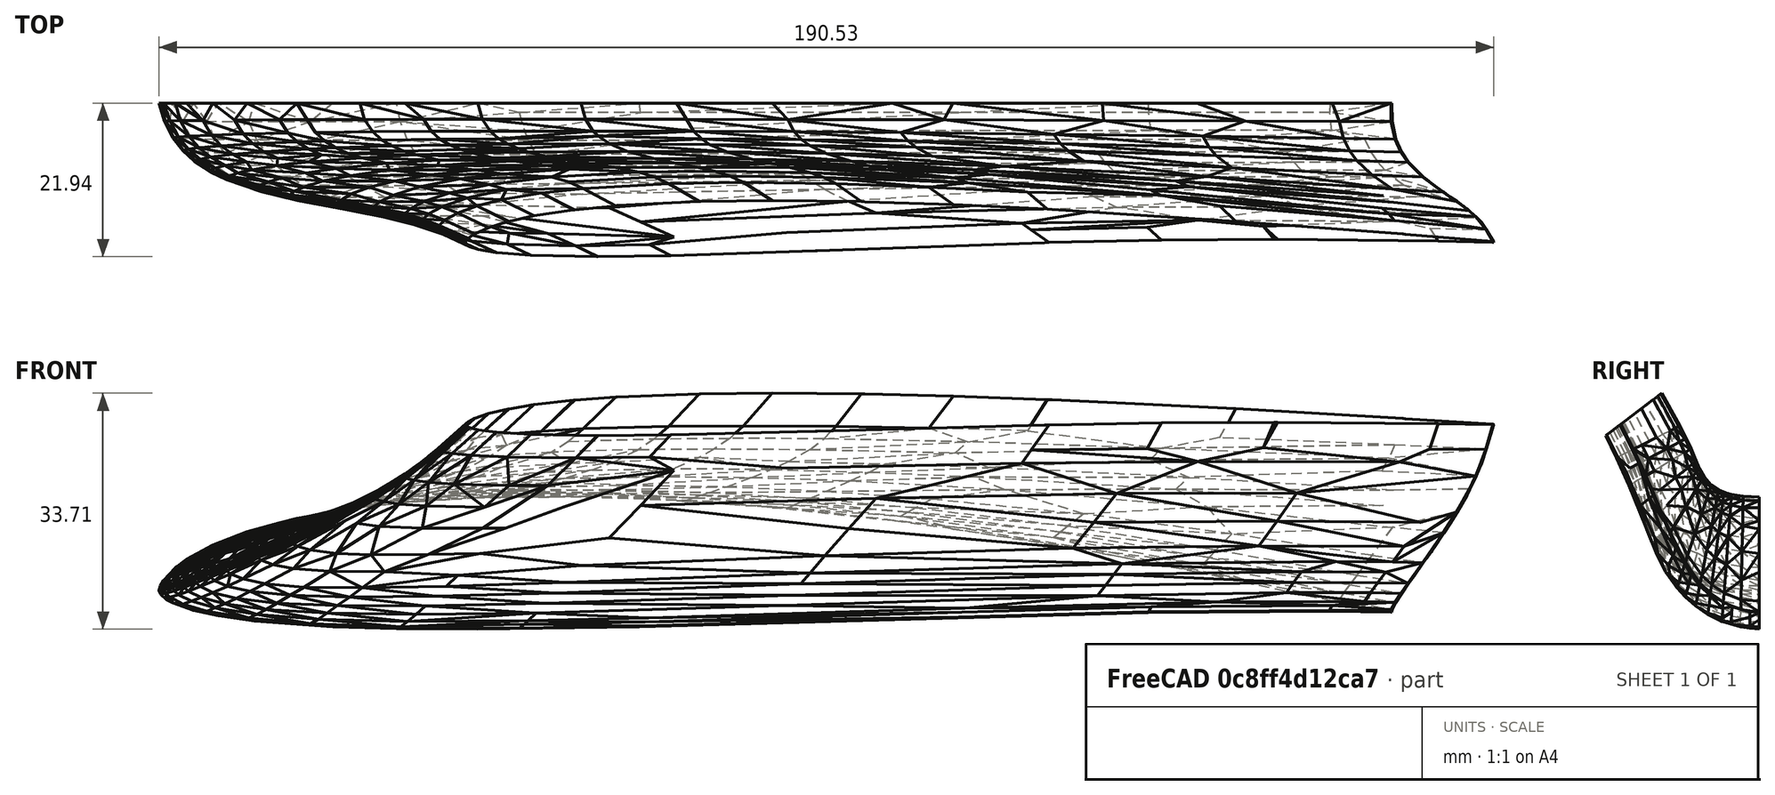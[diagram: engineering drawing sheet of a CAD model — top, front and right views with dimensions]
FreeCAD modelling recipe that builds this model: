
FCSTD DOCUMENT  (FreeCAD 0.19R24276 (Git))
Label: Con_left_winglet_alternative
License: All rights reserved
LicenseURL: http://en.wikipedia.org/wiki/All_rights_reserved
objects: Mesh::Feature×1, Sketcher::SketchObject×1, PartDesign::Body×1, Part::Extrusion×1, Part::Feature×1, Part::MultiCommon×1
note: 5 computed .brp shape members not serialized (recipe doc carries the construction recipe); baked Part::Feature solids carry a one-line shape summary decoded from their .brp

FEATURE [Mesh::Feature] Con_left_winglet_alternative
FEATURE [Sketcher::SketchObject] Sketch
  FullyConstrained = true
  MapMode = 5
  Placement = pos=(0,0,0) rot=(0.57735,0.57735,0.57735;2.0944rad)
  Support = -> [YZ_Plane]
  sketch-geometry (5):
    g0: LineSegment StartX=-958.452 StartY=44.13 StartZ=0 EndX=-927.93 EndY=67.13 EndZ=0
    g1: LineSegment StartX=-927.93 StartY=67.13 StartZ=0 EndX=-887.15 EndY=67.13 EndZ=0
    g2: LineSegment StartX=-887.15 StartY=67.13 StartZ=0 EndX=-887.15 EndY=23.57 EndZ=0
    g3: LineSegment StartX=-887.15 StartY=23.57 StartZ=0 EndX=-958.452 EndY=23.57 EndZ=0
    g4: LineSegment StartX=-958.452 StartY=23.57 StartZ=0 EndX=-958.452 EndY=44.13 EndZ=0
  constraints (15):
    c: Coincident(g0,g1)
    c: Horizontal(g1)
    c: Coincident(g1,g2)
    c: Vertical(g2)
    c: Coincident(g2,g3)
    c: Horizontal(g3)
    c: Coincident(g3,g4)
    c: Coincident(g4,g0)
    c: Vertical(g4)
    c: Angle(g-1,g0) = 0.645772
    c: DistanceX(g2,g-1) = 887.15
    c: DistanceY(g-1,g2) = 23.57
    c: DistanceY(g2,g2) = 43.56
    c: DistanceY(g4,g4) = 20.56
    c: DistanceX(g1,g1) = 40.78
FEATURE [PartDesign::Body] Body
  Group = -> [Sketch]
  Origin = -> Origin
FEATURE [Part::Extrusion] Extrude002  label="Extrude"
  Base = -> Sketch
  Dir = (1,-1e-16,1e-16)
  DirMode = 2
  FaceMakerClass = Part::FaceMakerBullseye
  LengthFwd = 500
  LengthRev = 0
  Solid = true
  Symmetric = false
FEATURE [Part::Feature] Con_left_winglet_alternative001
  shape: bbox 222.2 x 75.89 x 139.7 mm, 1118 faces, 0 solids (baked)
FEATURE [Part::MultiCommon] Common
  Shapes = -> [Extrude002,Con_left_winglet_alternative001]
